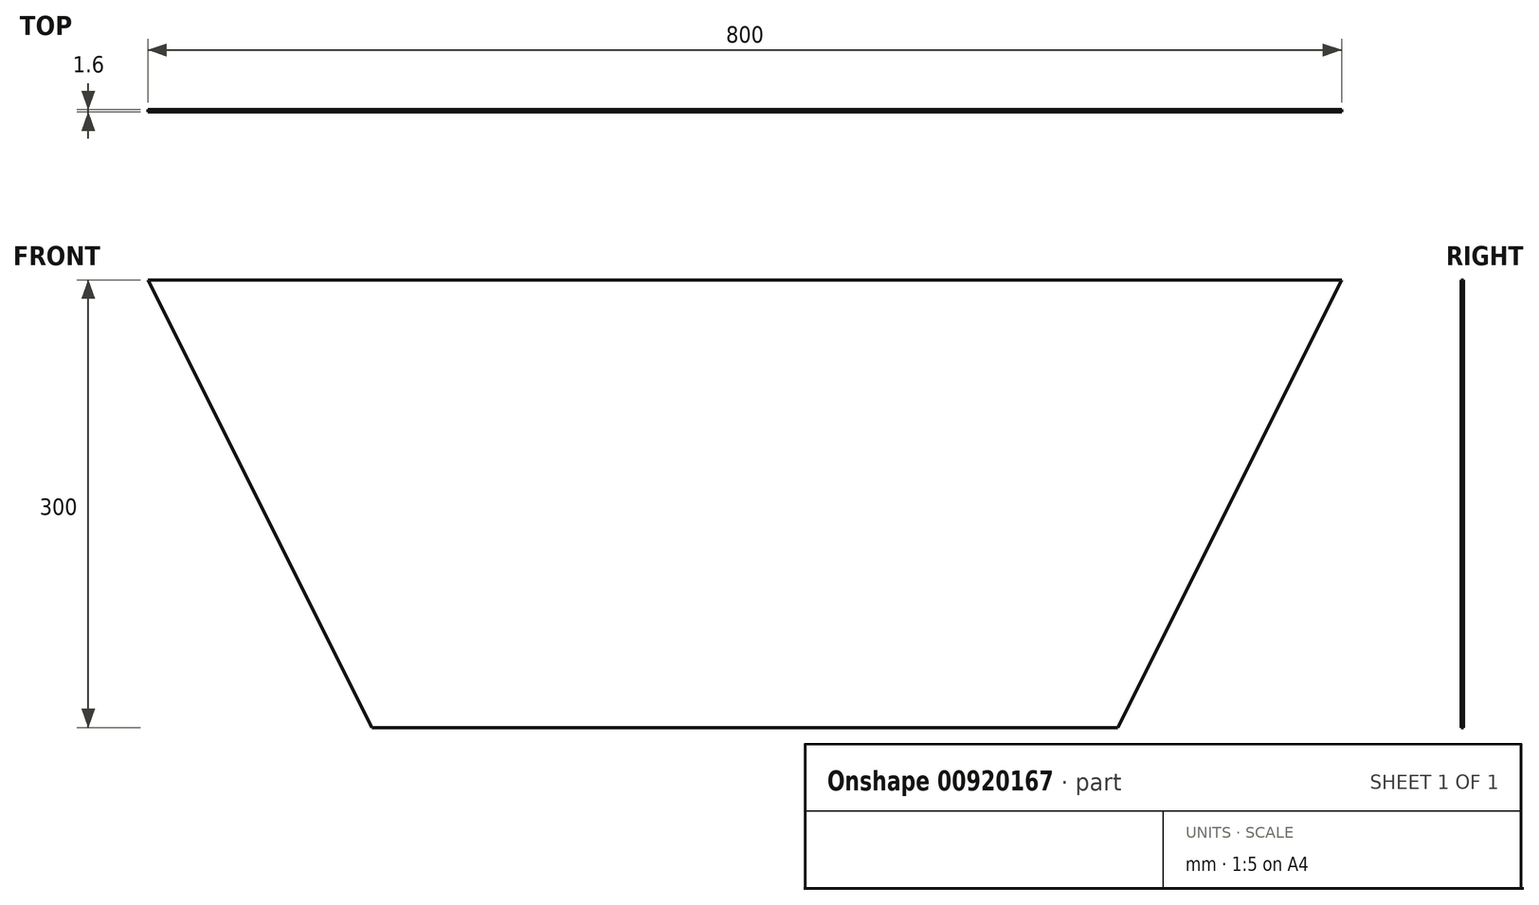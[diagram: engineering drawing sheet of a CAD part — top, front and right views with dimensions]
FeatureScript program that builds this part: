
annotation { "Feature Type Name" : "Feature", "Feature Type Description" : "" }
export const myFeature = defineFeature(function(context is Context, id is Id, definition is map)
    precondition{}
    {
        {
            var Q0;
            Q0=qCreatedBy(makeId("Front.planeOp"),FACE);
            var sketch = newSketch(context, id + "F0", { "sketchPlane" : qUnion([Q0])});
            skLineSegment(sketch, "E0", {"start": v(-250, -214.06) * mm, "end": v(250, -214.06) * mm});
            skLineSegment(sketch, "E1", {"start": v(399.2, 84.34) * mm, "end": v(250, -214.06) * mm});
            skLineSegment(sketch, "E2", {"start": v(-399.2, 84.34) * mm, "end": v(-250, -214.06) * mm});
            skLineSegment(sketch, "E3", {"start": v(-400, 85.94) * mm, "end": v(-399.2, 84.34) * mm});
            skLineSegment(sketch, "E4", {"start": v(399.2, 84.34) * mm, "end": v(400, 85.94) * mm});
            skLineSegment(sketch, "E5", {"start": v(400, 85.94) * mm, "end": v(-400, 85.94) * mm});
            skSolve(sketch);
        }
        {
            var Q0;
            Q0 = qSketchRegion(id + "F0", true);
            extrude(context, id + "F1", {"entities" : qUnion([Q0]), "depth" : 1.6 * mm, "offsetDistance" : 25 * mm});
        }
    });
